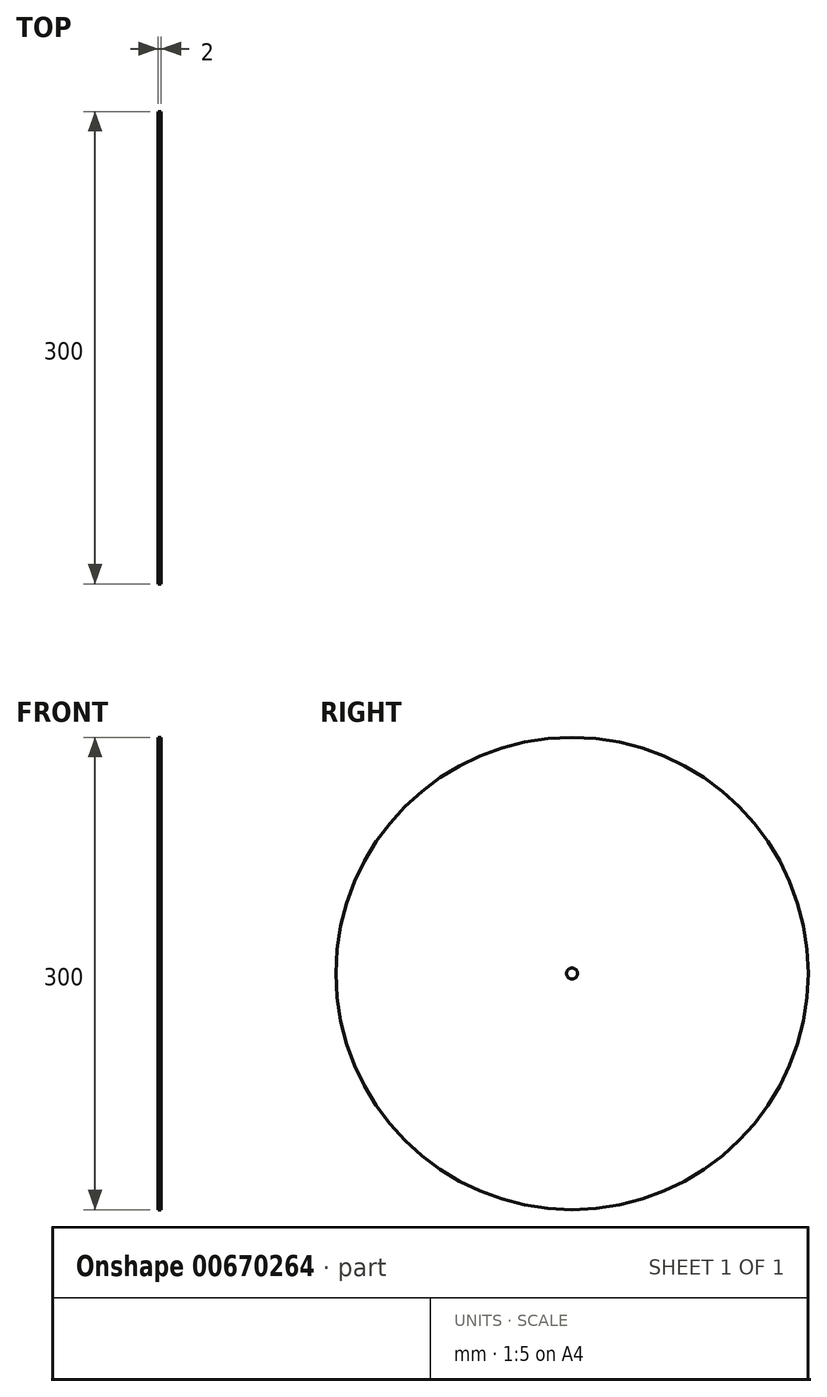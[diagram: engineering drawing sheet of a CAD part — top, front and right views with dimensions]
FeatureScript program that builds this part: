
annotation { "Feature Type Name" : "Feature", "Feature Type Description" : "" }
export const myFeature = defineFeature(function(context is Context, id is Id, definition is map)
    precondition{}
    {
        {
            var Q0;
            Q0=qCreatedBy(makeId("Right.planeOp"),FACE);
            var sketch = newSketch(context, id + "F0", { "sketchPlane" : qUnion([Q0])});
            skCircle(sketch, "E0", {"center": v(0, 0) * mm, "radius": 150 * mm});
            skCircle(sketch, "E1", {"center": v(0, 0) * mm, "radius": 3.5 * mm});
            skSolve(sketch);
        }
        {
            var Q0;
            Q0=makeQuery(id+"F0.imprint","IMPRINT",FACE,{"disambiguationData":[TD([[makeQuery(id+"F0.imprint","IMPRINT",EDGE,{"derivedFrom":sQuery(id+"F0.wireOp",EDGE,"E0")}),1.0]])]});
            extrude(context, id + "F1", {"entities" : qUnion([Q0]), "depth" : 2 * mm, "offsetDistance" : 25 * mm});
        }
    });
